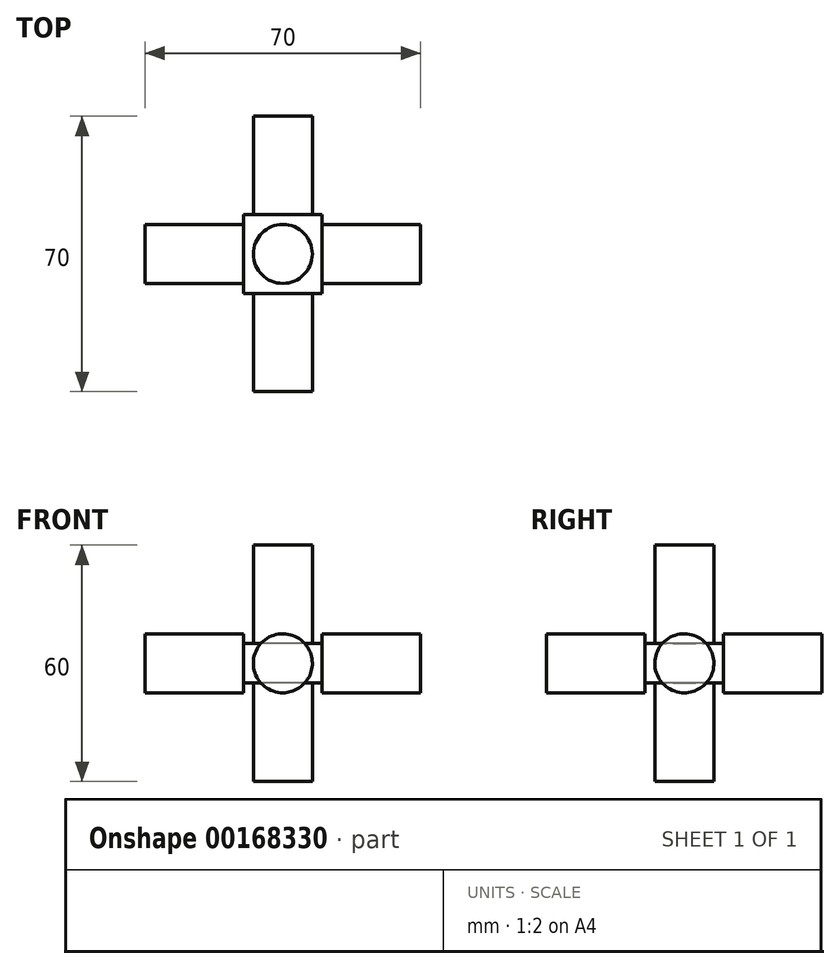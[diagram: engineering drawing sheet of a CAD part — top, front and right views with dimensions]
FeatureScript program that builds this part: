
annotation { "Feature Type Name" : "Feature", "Feature Type Description" : "" }
export const myFeature = defineFeature(function(context is Context, id is Id, definition is map)
    precondition{}
    {
        {
            var Q0;
            Q0=qCreatedBy(makeId("Top.planeOp"),FACE);
            var sketch = newSketch(context, id + "F0", { "sketchPlane" : qUnion([Q0])});
            skLineSegment(sketch, "E0.bottom", {"start": v(10, 10) * mm, "end": v(-10, 10) * mm});
            skLineSegment(sketch, "E0.top", {"start": v(10, -10) * mm, "end": v(-10, -10) * mm});
            skLineSegment(sketch, "E0.left", {"start": v(10, 10) * mm, "end": v(10, -10) * mm});
            skLineSegment(sketch, "E0.right", {"start": v(-10, 10) * mm, "end": v(-10, -10) * mm});
            skPoint(sketch, "E0.middle", {"position": v(0, 0) * mm});
            skSolve(sketch);
        }
        {
            var Q0;
            Q0=qSketchRegion(id+"F0",true);
            extrude(context, id + "F1", {"entities" : qUnion([Q0]), "depth" : 10 * mm});
        }
        {
            var Q0;
            Q0=makeQuery(id+"F1.opExtrude","CAP_FACE",FACE,{"disambiguationData":[OSD([sQuery(id+"F0.wireOp",EDGE,"E0.bottom"),sQuery(id+"F0.wireOp",EDGE,"E0.top"),sQuery(id+"F0.wireOp",EDGE,"E0.left"),sQuery(id+"F0.wireOp",EDGE,"E0.right")])],"isStart":false});
            var sketch = newSketch(context, id + "F2", { "sketchPlane" : qUnion([Q0])});
            skCircle(sketch, "E1", {"center": v(0, 0) * mm, "radius": 7.5 * mm});
            skSolve(sketch);
        }
        {
            var Q0;
            Q0=makeQuery(id+"F1.opExtrude","SWEPT_FACE",FACE,{"disambiguationData":[OSD([sQuery(id+"F0.wireOp",EDGE,"E0.left")])]});
            var sketch = newSketch(context, id + "F3", { "sketchPlane" : qUnion([Q0])});
            skCircle(sketch, "E2", {"center": v(0, 5) * mm, "radius": 7.5 * mm});
            skPoint(sketch, "E2.centerSnap0", {"position": v(10, 5) * mm});
            skSolve(sketch);
        }
        {
            var Q0;
            Q0=makeQuery(id+"F1.opExtrude","SWEPT_FACE",FACE,{"disambiguationData":[OSD([sQuery(id+"F0.wireOp",EDGE,"E0.top")])]});
            var sketch = newSketch(context, id + "F4", { "sketchPlane" : qUnion([Q0])});
            skCircle(sketch, "E3", {"center": v(0, 5) * mm, "radius": 7.5 * mm});
            skPoint(sketch, "E3.centerSnap0", {"position": v(10, 5) * mm});
            skSolve(sketch);
        }
        {
            var Q0;
            Q0=makeQuery(id+"F1.opExtrude","SWEPT_FACE",FACE,{"disambiguationData":[OSD([sQuery(id+"F0.wireOp",EDGE,"E0.right")])]});
            var sketch = newSketch(context, id + "F5", { "sketchPlane" : qUnion([Q0])});
            skCircle(sketch, "E4", {"center": v(0, 5) * mm, "radius": 7.5 * mm});
            skPoint(sketch, "E4.centerSnap0", {"position": v(10, 5) * mm});
            skSolve(sketch);
        }
        {
            var Q0;
            Q0=makeQuery(id+"F1.opExtrude","SWEPT_FACE",FACE,{"disambiguationData":[OSD([sQuery(id+"F0.wireOp",EDGE,"E0.bottom")])]});
            var sketch = newSketch(context, id + "F6", { "sketchPlane" : qUnion([Q0])});
            skCircle(sketch, "E5", {"center": v(0, 5) * mm, "radius": 7.5 * mm});
            skPoint(sketch, "E5.centerSnap0", {"position": v(10, 5) * mm});
            skSolve(sketch);
        }
        {
            var Q0;
            Q0=makeQuery(id+"F0.imprint","IMPRINT",FACE,{"disambiguationData":[TD([[makeQuery(id+"F0.imprint","IMPRINT",EDGE,{"derivedFrom":sQuery(id+"F0.wireOp",EDGE,"E0.bottom")}),1.0]])]});
            var sketch = newSketch(context, id + "F7", { "sketchPlane" : qUnion([Q0])});
            skCircle(sketch, "E6", {"center": v(0, 0) * mm, "radius": 7.5 * mm});
            skSolve(sketch);
        }
        {
            var Q0;
            Q0=qSketchRegion(id+"F2",true);
            extrude(context, id + "F8", {"entities" : qUnion([Q0]), "operationType" : NewBodyOperationType.ADD, "depth" : 25 * mm});
        }
        {
            var Q0;
            Q0=qSketchRegion(id+"F3",true);
            extrude(context, id + "F9", {"entities" : qUnion([Q0]), "operationType" : NewBodyOperationType.ADD, "depth" : 25 * mm});
        }
        {
            var Q0;
            Q0=qSketchRegion(id+"F4",true);
            extrude(context, id + "F10", {"entities" : qUnion([Q0]), "operationType" : NewBodyOperationType.ADD, "depth" : 25 * mm});
        }
        {
            var Q0;
            Q0=qSketchRegion(id+"F5",true);
            extrude(context, id + "F11", {"entities" : qUnion([Q0]), "operationType" : NewBodyOperationType.ADD, "depth" : 25 * mm});
        }
        {
            var Q0;
            Q0=qSketchRegion(id+"F6",true);
            extrude(context, id + "F12", {"entities" : qUnion([Q0]), "operationType" : NewBodyOperationType.ADD, "depth" : 25 * mm});
        }
        {
            var Q0;
            Q0=qSketchRegion(id+"F7",true);
            extrude(context, id + "F13", {"entities" : qUnion([Q0]), "operationType" : NewBodyOperationType.ADD, "oppositeDirection" : true, "depth" : 25 * mm});
        }
    });
